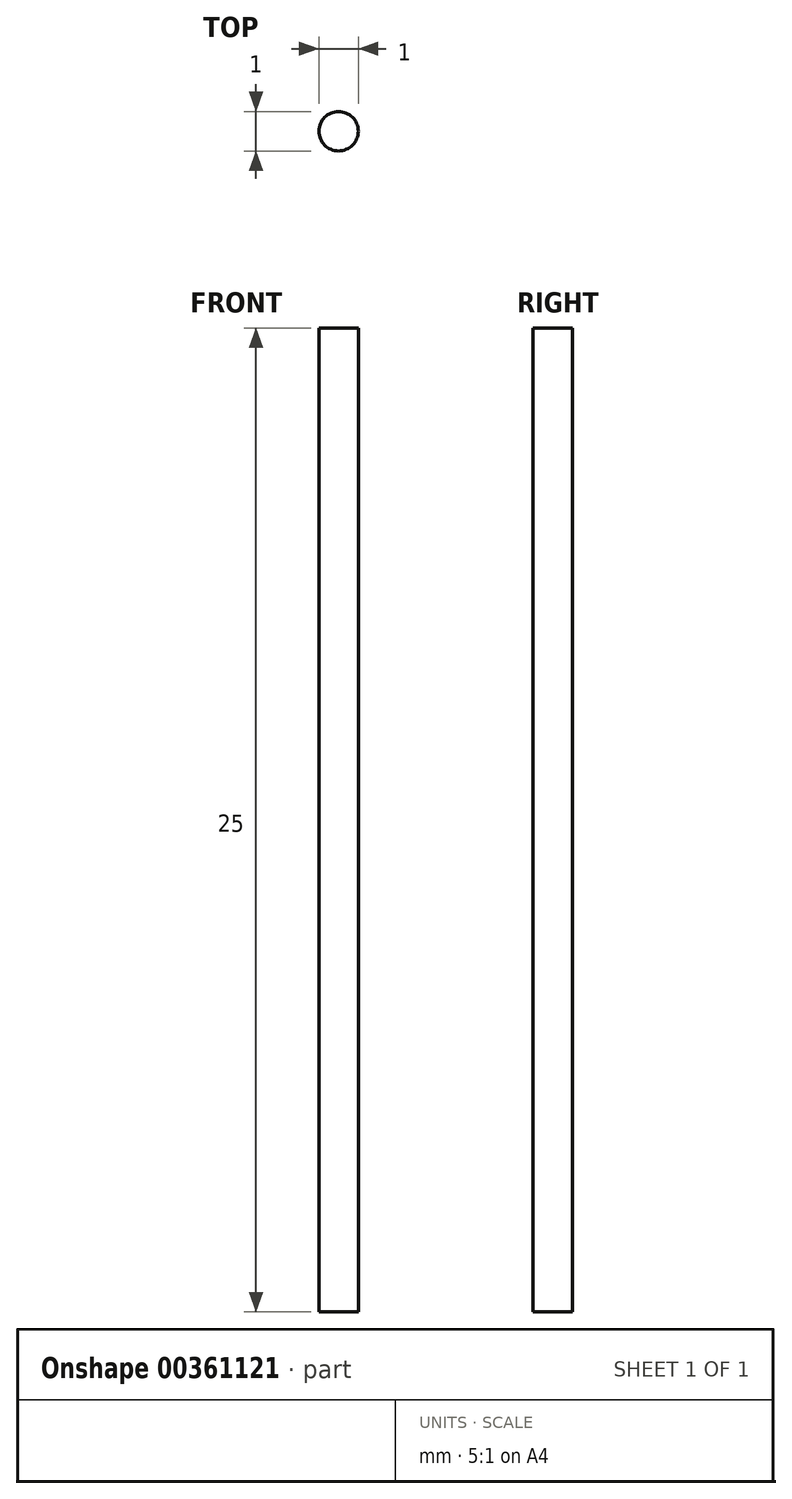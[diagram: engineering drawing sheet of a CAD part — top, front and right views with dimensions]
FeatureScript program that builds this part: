
annotation { "Feature Type Name" : "Feature", "Feature Type Description" : "" }
export const myFeature = defineFeature(function(context is Context, id is Id, definition is map)
    precondition{}
    {
        {
            var Q0;
            Q0=qCreatedBy(makeId("Top.planeOp"),FACE);
            var sketch = newSketch(context, id + "F0", { "sketchPlane" : qUnion([Q0])});
            skCircle(sketch, "E0", {"center": v(0, 0) * mm, "radius": 0.5 * mm});
            skSolve(sketch);
        }
        {
            var Q0;
            Q0 = qSketchRegion(id + "F0", true);
            extrude(context, id + "F1", {"entities" : qUnion([Q0]), "depth" : 25 * mm});
        }
    });
